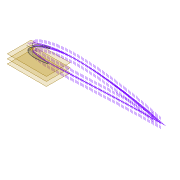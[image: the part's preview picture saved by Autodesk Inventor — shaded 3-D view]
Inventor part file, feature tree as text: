
AUTODESK INVENTOR PART (.ipt)
format: ipt  version: 2022 (Build 260153000, 153)  size: 403,456 bytes
history: native  units: mm
features: extrude x8, sketch x8, projected_geometry x4, plane x3, thicken_offset x2, shell x1, revolve x1
ambient origin geometry x8: Origin, YZ Plane, XZ Plane, XY Plane, X Axis, Y Axis, Z Axis, Center Point
bodies: Solid1 (feature_tree)
feature tree (27):
  extrude  "Extrusion1"  Depth=1.0mm
  shell  "Shell1"  Thickness=80.0mm
  extrude  "Extrusion16"  Depth=10.0mm
  revolve  "Revolution2"  [1 undecoded]
  extrude  "Extrusion17"  Depth=100.0mm TaperAngle=0.0deg
  plane  "Work Plane4"
  plane  "Work Plane5"
  plane  "Work Plane6"
  sketch  "Sketch41"  dims[d176=36.0mm d177=100.0mm d178=0.0mm]
  extrude  "Extrusion18"  Depth=100.0mm TaperAngle=0.0deg
  extrude  "Extrusion22"  Depth=2.4mm
  extrude  "Extrusion20"  Depth=2.4mm
  thicken_offset  "Thicken2"
  thicken_offset  "Thicken3"
  extrude  "Extrusion23"  Depth=2.5mm TaperAngle=0.0deg
  extrude  "Extrusion24"  Depth=2.5mm TaperAngle=0.0deg
  sketch  "Sketch3"  dims[d0=1.0mm d1=0.0mm d2=1.0mm d159=80.0mm]
  sketch  "Sketch37"  dims[d160=10.0mm d161=0.0mm d163=1.745329mm]
  sketch  "Sketch39"  dims[d164=1.0mm d165=0.0mm d166=6.454mm d167=16.2mm d168=-16.2mm]
  projected_geometry  "Projected Loop21"
  sketch  "Sketch40"  dims[d169=33.2mm d170=100.0mm d171=0.0mm]
  projected_geometry  "Projected Loop22"
  sketch  "Sketch44"  dims[d181=2.4mm d182=2.4mm]
  sketch  "Sketch45"  dims[d183=2.4mm d184=2.4mm]
  projected_geometry  "Projected Loop24"
  sketch  "Sketch46"  dims[d187=4.0mm d188=15.6mm d189=0.0mm d190=13.1mm d191=0.0mm d192=1.745329mm d193=2.5mm d194=0.0mm]
  projected_geometry  "Projected Loop25"
note: 1 required parameter value undecoded (feature->parameter linkage not recoverable at this tier; creation-order binding heuristic only, values carry confidence <= 0.55)
